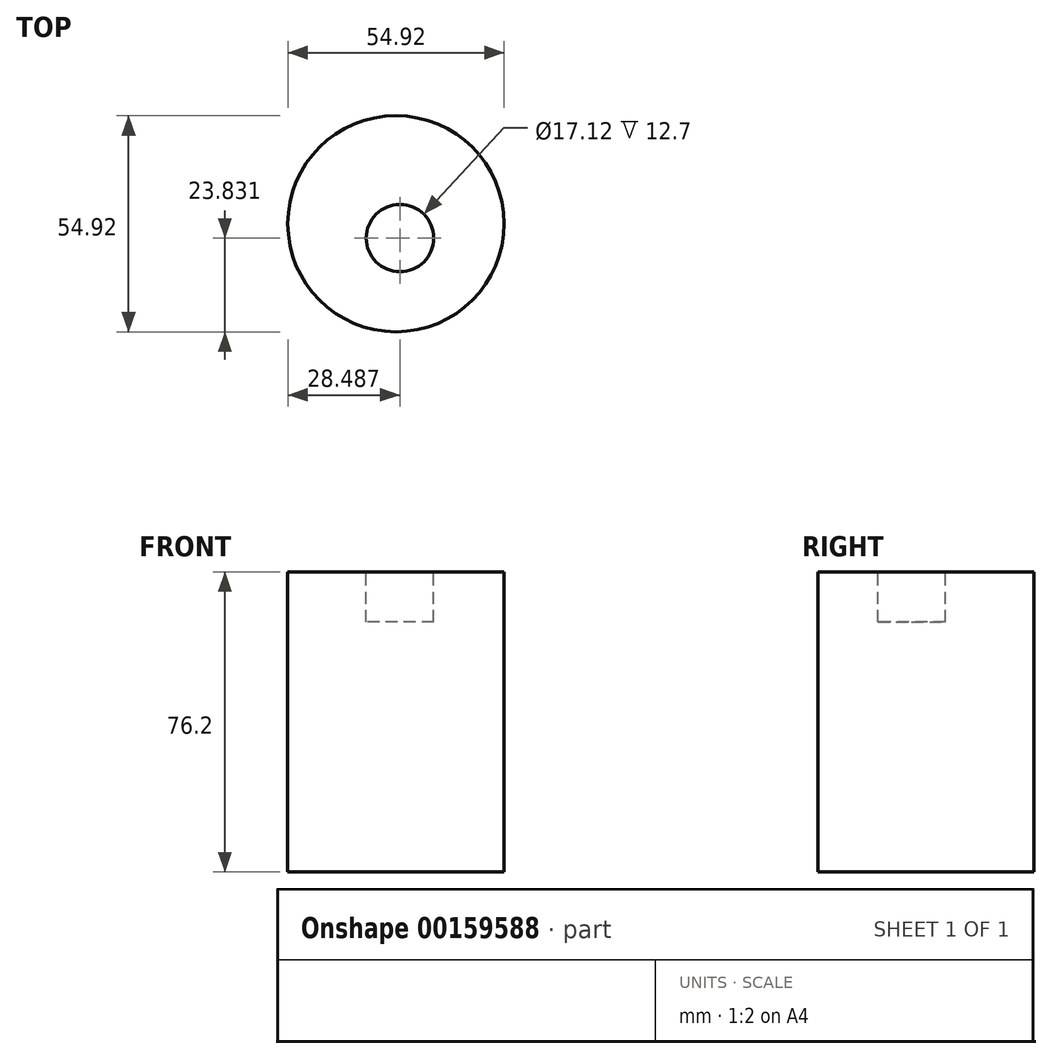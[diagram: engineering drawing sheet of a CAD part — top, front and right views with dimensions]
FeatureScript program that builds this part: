
annotation { "Feature Type Name" : "Feature", "Feature Type Description" : "" }
export const myFeature = defineFeature(function(context is Context, id is Id, definition is map)
    precondition{}
    {
        {
            var Q0;
            Q0=qCreatedBy(makeId("Top.planeOp"),FACE);
            var sketch = newSketch(context, id + "F0", { "sketchPlane" : qUnion([Q0])});
            skCircle(sketch, "E0", {"center": v(-99.42, -83.52) * mm, "radius": 27.46 * mm});
            skSolve(sketch);
        }
        {
            var Q0;
            Q0=makeQuery(id+"F0.imprint","IMPRINT",FACE,{"disambiguationData":[TD([[makeQuery(id+"F0.imprint","IMPRINT",EDGE,{"derivedFrom":sQuery(id+"F0.wireOp",EDGE,"E0")}),1.0]])]});
            extrude(context, id + "F1", {"entities" : qUnion([Q0]), "depth" : 76.2 * mm});
        }
        {
            var Q0;
            Q0=makeQuery(id+"F1.opExtrude","CAP_FACE",FACE,{"disambiguationData":[OSD([sQuery(id+"F0.wireOp",EDGE,"E0")])],"isStart":false});
            var sketch = newSketch(context, id + "F2", { "sketchPlane" : qUnion([Q0])});
            skCircle(sketch, "E1", {"center": v(-98.4, -87.15) * mm, "radius": 8.56 * mm});
            skSolve(sketch);
        }
        {
            var Q0;
            Q0=makeQuery(id+"F2.imprint","IMPRINT",FACE,{"disambiguationData":[TD([[makeQuery(id+"F2.imprint","IMPRINT",EDGE,{"derivedFrom":sQuery(id+"F2.wireOp",EDGE,"E1")}),1.0]])]});
            var Q1;
            Q1=sQuery(id+"F2.wireOp",EDGE,"E1");
            extrude(context, id + "F3", {"entities" : qUnion([Q0]), "operationType" : NewBodyOperationType.REMOVE, "surfaceEntities" : qUnion([Q1]), "oppositeDirection" : true, "depth" : 12.7 * mm});
        }
    });
